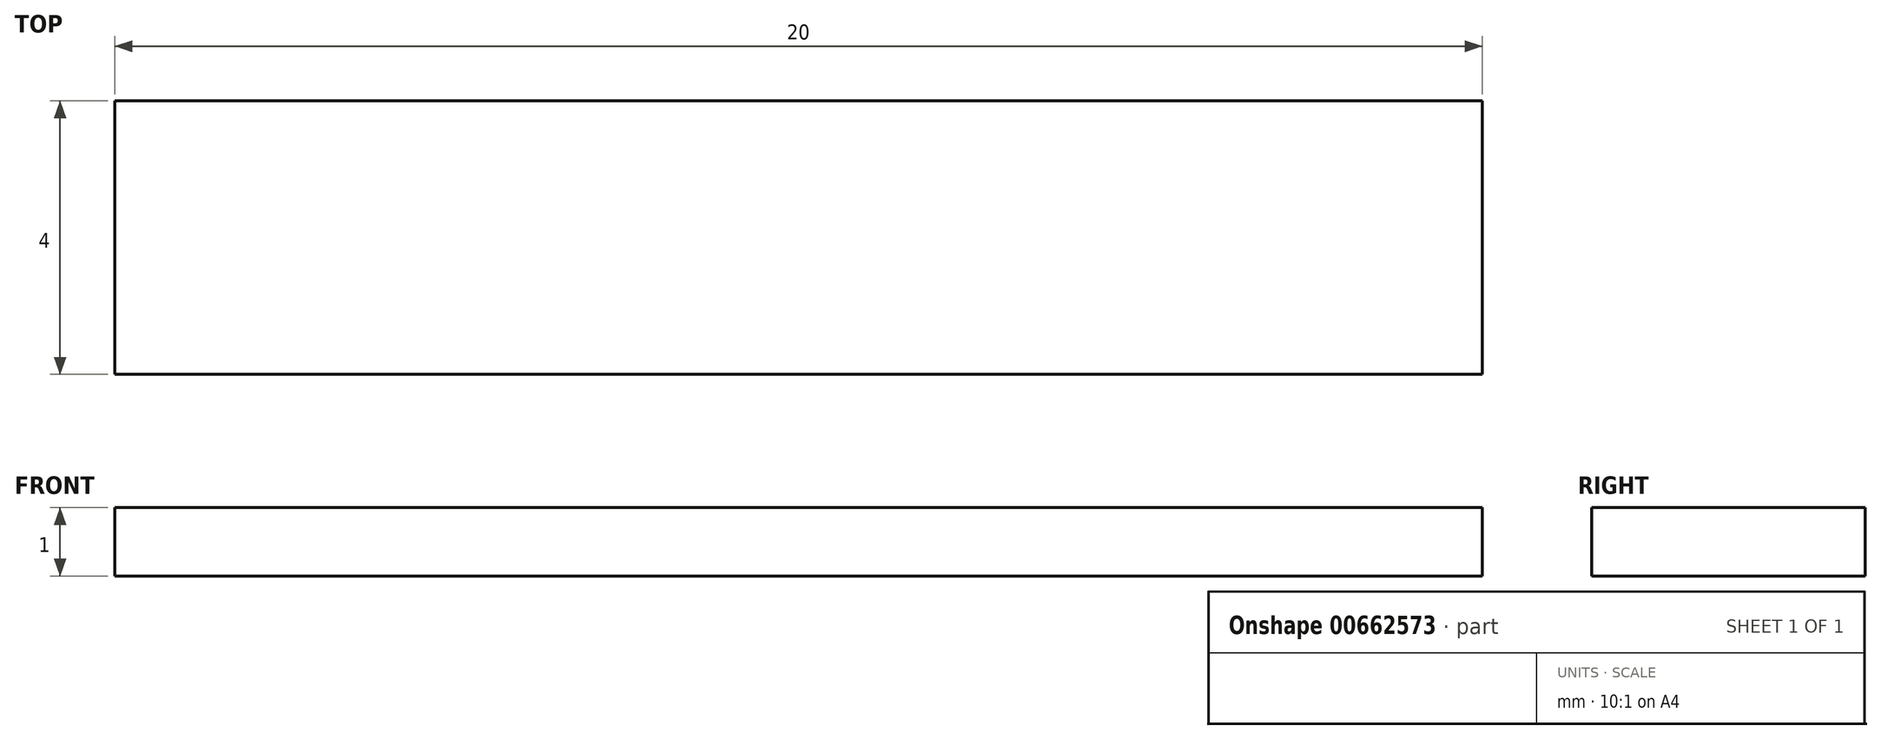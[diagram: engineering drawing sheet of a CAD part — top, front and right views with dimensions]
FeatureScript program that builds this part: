
annotation { "Feature Type Name" : "Feature", "Feature Type Description" : "" }
export const myFeature = defineFeature(function(context is Context, id is Id, definition is map)
    precondition{}
    {
        {
            var Q0;
            Q0=qCreatedBy(makeId("Top.planeOp"),FACE);
            var sketch = newSketch(context, id + "F0", { "sketchPlane" : qUnion([Q0])});
            skLineSegment(sketch, "E0", {"start": v(0, 0) * mm, "end": v(20, 0) * mm});
            skLineSegment(sketch, "E1", {"start": v(20, 0) * mm, "end": v(20, 4) * mm});
            skLineSegment(sketch, "E2", {"start": v(20, 4) * mm, "end": v(0, 4) * mm});
            skLineSegment(sketch, "E3", {"start": v(0, 4) * mm, "end": v(0, 0) * mm});
            skSolve(sketch);
        }
        {
            var Q0;
            Q0=makeQuery(id+"F0.imprint","IMPRINT",FACE,{"disambiguationData":[TD([[makeQuery(id+"F0.imprint","IMPRINT",EDGE,{"derivedFrom":sQuery(id+"F0.wireOp",EDGE,"E0")}),1.0]])]});
            extrude(context, id + "F1", {"entities" : qUnion([Q0]), "depth" : 1 * mm, "offsetDistance" : 25 * mm});
        }
    });
